# Revit family: UF-653-004_D83-I2L
name_source: partatom
category: Equipement spécialisé
units: mm (PartAtom-declared; Revit-internal decimal feet)

## family parameters
Basée sur le plan de construction = Non
Cote de connecteur circulaire = Utiliser le diamètre
Couper avec des vides une fois chargée = Non
Numéro OmniClass = 23.85.50.31.11
Partagée = Non
Point de calcul de pièce = Non
Titre OmniClass = Door Entry Telephones
Toujours verticalement = Oui
Type d'élément = Normal

## types (1)
- Norme
    Description = GAMME 2VOICE
    Elévation par défaut = 0 mm  [stored 0 ft]
    Fabricant = URMET FRANCE
    Modèle = D83-I2L
    URL = https://www.urmet.fr
    d0 = 0 mm  [stored 0 ft]
    d1 = 0 mm  [stored 0 ft]
    d101 = 0 mm  [stored 0 ft]
    d102 = 0 mm  [stored 0 ft]
    d103 = 0 mm  [stored 0 ft]
    d104 = 0 mm  [stored 0 ft]
    d105 = 0 mm  [stored 0 ft]
    d106 = 0 mm  [stored 0 ft]
    d107 = 0 mm  [stored 0 ft]
    d108 = 0 mm  [stored 0 ft]
    d113 = 0 mm  [stored 0 ft]
    d117 = 0 mm  [stored 0 ft]
    d118 = 0 mm  [stored 0 ft]
    d120 = 0 mm  [stored 0 ft]
    d121 = 0 mm  [stored 0 ft]
    d122 = 0 mm  [stored 0 ft]
    d2 = 0 mm  [stored 0 ft]
    d3 = 0 mm  [stored 0 ft]
    d30 = 0 mm  [stored 0 ft]
    d31 = 0 mm  [stored 0 ft]
    d32 = 0 mm  [stored 0 ft]
    d34 = 0 mm  [stored 0 ft]
    d35 = 0 mm  [stored 0 ft]
    d36 = 0 mm  [stored 0 ft]
    d37 = 0 mm  [stored 0 ft]
    d38 = 0 mm  [stored 0 ft]
    d39 = 0 mm  [stored 0 ft]
    d41 = 0 mm  [stored 0 ft]
    d42 = 0 mm  [stored 0 ft]
    d55 = 0 mm  [stored 0 ft]
    d56 = 0 mm  [stored 0 ft]
    d57 = 0 mm  [stored 0 ft]
    d60 = 0 mm  [stored 0 ft]
    d63 = 0 mm  [stored 0 ft]
    d73 = 0 mm  [stored 0 ft]
    d74 = 0 mm  [stored 0 ft]
    d75 = 0 mm  [stored 0 ft]
    d76 = 0 mm  [stored 0 ft]
    d77 = 0 mm  [stored 0 ft]
    d78 = 0 mm  [stored 0 ft]
    d79 = 0 mm  [stored 0 ft]
    d80 = 0 mm  [stored 0 ft]
    d81 = 0 mm  [stored 0 ft]
    d82 = 0 mm  [stored 0 ft]
    d84 = 0 mm  [stored 0 ft]
    d85 = 0 mm  [stored 0 ft]
    d86 = 0 mm  [stored 0 ft]
    d87 = 0 mm  [stored 0 ft]
    d88 = 0 mm  [stored 0 ft]
    d89 = 0 mm  [stored 0 ft]
    d90 = 45,00°
    d91 = 45,00°
    d92 = 0 mm  [stored 0 ft]
    d93 = 0 mm  [stored 0 ft]
    d94 = 0 mm  [stored 0 ft]
    d96 = 0 mm  [stored 0 ft]
    d97 = 0 mm  [stored 0 ft]
    d98 = 0 mm  [stored 0 ft]
    d99 = 0 mm  [stored 0 ft]

note: [stored X ft] marks values corroborated as IEEE doubles in the binary element streams (Revit-internal decimal feet)
